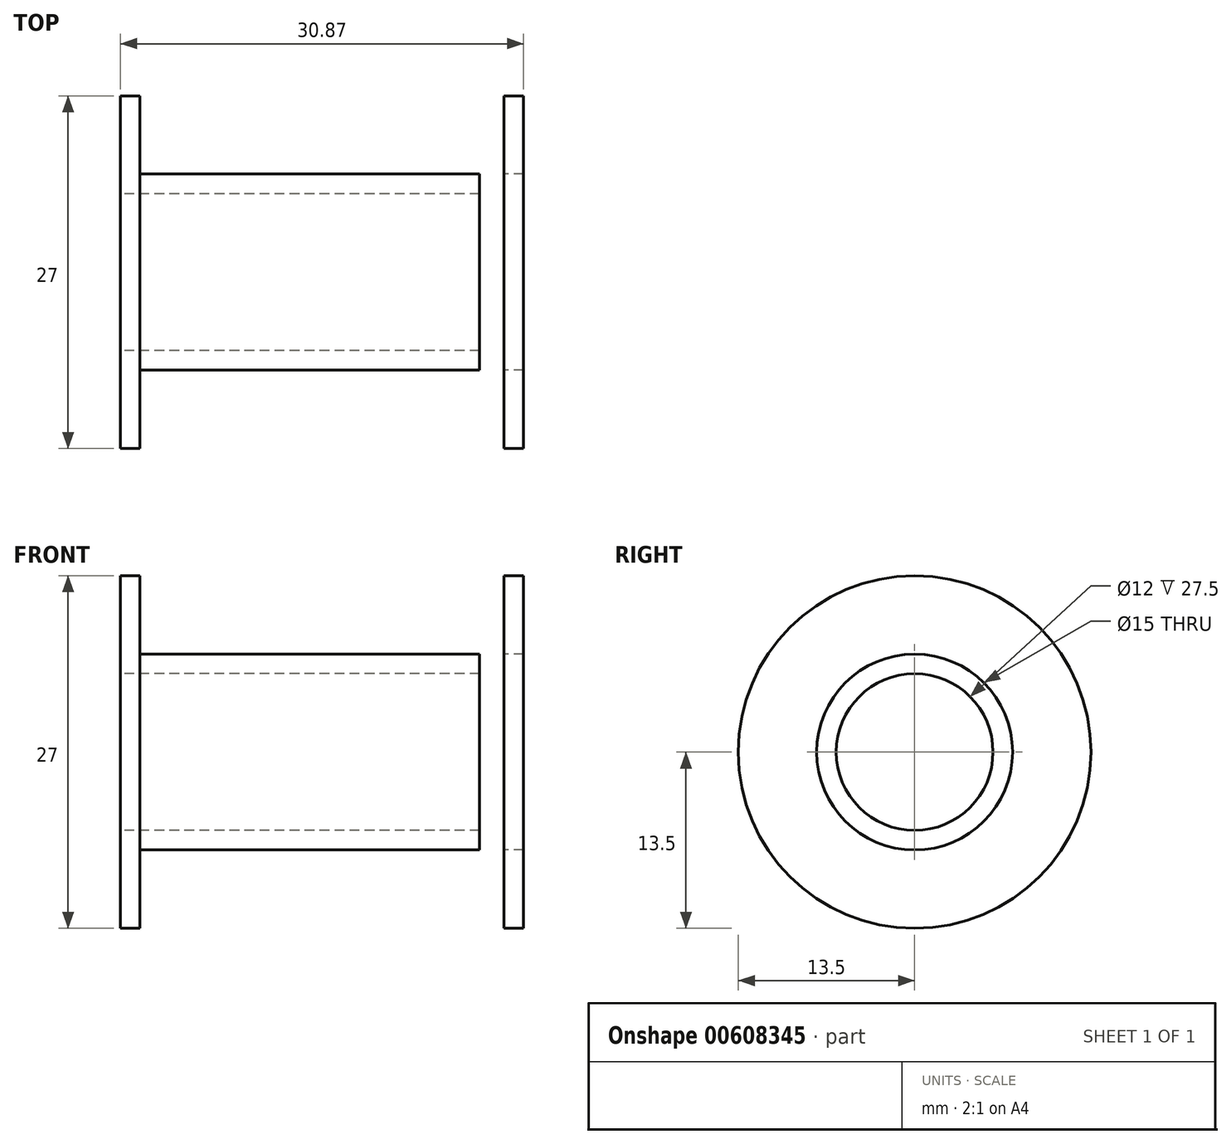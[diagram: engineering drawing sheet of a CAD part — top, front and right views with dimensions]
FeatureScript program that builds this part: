
annotation { "Feature Type Name" : "Feature", "Feature Type Description" : "" }
export const myFeature = defineFeature(function(context is Context, id is Id, definition is map)
    precondition{}
    {
        {
            var Q0;
            Q0=qCreatedBy(makeId("Front.planeOp"),FACE);
            var sketch = newSketch(context, id + "F0", { "sketchPlane" : qUnion([Q0])});
            skLineSegment(sketch, "E0", {"start": v(14.56, 6) * mm, "end": v(-12.94, 6) * mm});
            skLineSegment(sketch, "E1", {"start": v(-12.94, 6) * mm, "end": v(-12.94, 13.5) * mm});
            skLineSegment(sketch, "E2", {"start": v(-12.94, 13.5) * mm, "end": v(-11.44, 13.5) * mm});
            skLineSegment(sketch, "E3", {"start": v(-11.44, 13.5) * mm, "end": v(-11.44, 7.5) * mm});
            skLineSegment(sketch, "E4", {"start": v(-11.44, 7.5) * mm, "end": v(14.56, 7.5) * mm});
            skLineSegment(sketch, "E5", {"start": v(14.56, 7.5) * mm, "end": v(14.56, 6) * mm});
            skLineSegment(sketch, "E6", {"start": v(-48.15, 0) * mm, "end": v(45.4, 0) * mm});
            skLineSegment(sketch, "E7.bottom", {"start": v(16.43, 7.5) * mm, "end": v(17.93, 7.5) * mm});
            skLineSegment(sketch, "E7.top", {"start": v(16.43, 13.5) * mm, "end": v(17.93, 13.5) * mm});
            skLineSegment(sketch, "E7.left", {"start": v(16.43, 7.5) * mm, "end": v(16.43, 13.5) * mm});
            skLineSegment(sketch, "E7.right", {"start": v(17.93, 7.5) * mm, "end": v(17.93, 13.5) * mm});
            skLineSegment(sketch, "E8", {"start": v(-12.94, 13.5) * mm, "end": v(37.47, 13.5) * mm, "construction": true});
            skLineSegment(sketch, "E9", {"start": v(-11.44, 7.5) * mm, "end": v(38.48, 7.5) * mm, "construction": true});
            skSolve(sketch);
        }
        {
            var Q0;
            Q0 = qSketchRegion(id + "F0", true);
            var Q1;
            Q1=sQuery(id+"F0.wireOp",EDGE,"E6");
            revolve(context, id + "F1", {"surfaceOperationType" : NewSurfaceOperationType.NEW, "entities" : qUnion([Q0]), "axis" : qUnion([Q1]), "revolveType" : RevolveType.FULL});
        }
    });
